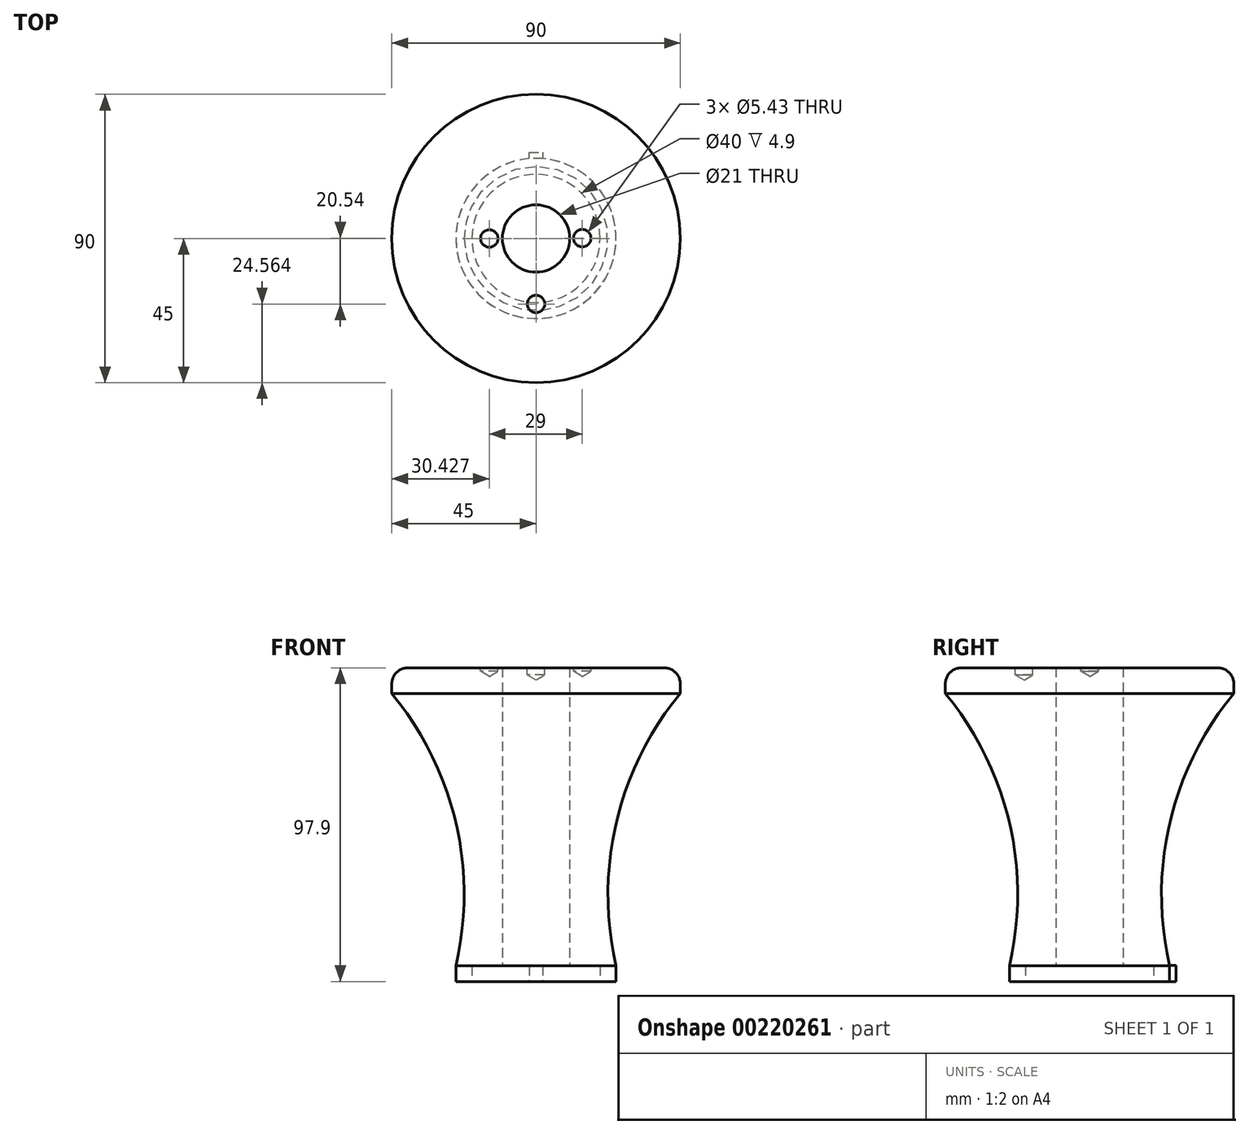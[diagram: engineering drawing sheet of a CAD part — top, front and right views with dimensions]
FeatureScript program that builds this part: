
annotation { "Feature Type Name" : "Feature", "Feature Type Description" : "" }
export const myFeature = defineFeature(function(context is Context, id is Id, definition is map)
    precondition{}
    {
        {
            var Q0;
            Q0=qCreatedBy(makeId("Front.planeOp"),FACE);
            var sketch = newSketch(context, id + "F0", { "sketchPlane" : qUnion([Q0])});
            skLineSegment(sketch, "E0", {"start": v(25, 0) * mm, "end": v(4, 0) * mm});
            skLineSegment(sketch, "E1", {"start": v(4, 0) * mm, "end": v(4, 60) * mm});
            skLineSegment(sketch, "E2", {"start": v(10, 85) * mm, "end": v(45, 85) * mm});
            skArc(sketch, "E3", {"start": v(45, 85) * mm, "mid": v(25.06, 44.84) * mm, "end": v(25, 0) * mm});
            skArc(sketch, "E4", {"start": v(10, 85) * mm, "mid": v(5.52, 72.85) * mm, "end": v(4, 60) * mm});
            skSolve(sketch);
        }
        {
            var Q0;
            Q0=qCreatedBy(makeId("Front.planeOp"),FACE);
            var sketch = newSketch(context, id + "F1", { "sketchPlane" : qUnion([Q0])});
            skLineSegment(sketch, "E5", {"start": v(0, 0) * mm, "end": v(0, 50.34) * mm});
            skSolve(sketch);
        }
        {
            var Q0;
            Q0=makeQuery(id+"F0.imprint","IMPRINT",FACE,{"disambiguationData":[TD([[makeQuery(id+"F0.imprint","IMPRINT",EDGE,{"derivedFrom":sQuery(id+"F0.wireOp",EDGE,"E0")}),-1.0]])]});
            var Q1;
            Q1=sQuery(id+"F1.wireOp",EDGE,"E5");
            revolve(context, id + "F2", {"entities" : qUnion([Q0]), "axis" : qUnion([Q1]), "revolveType" : RevolveType.FULL});
        }
        {
            var Q0;
            Q0=makeQuery(id+"F2.opRevolve","SWEPT_FACE",FACE,{"disambiguationData":[OSD([sQuery(id+"F0.wireOp",EDGE,"E0")])]});
            extrude(context, id + "F3", {"entities" : qUnion([Q0]), "operationType" : NewBodyOperationType.ADD, "depth" : 4.9 * mm});
        }
        {
            var Q0;
            Q0=makeQuery(id+"F3.opExtrude","CAP_FACE",FACE,{"disambiguationData":[OSD([sQuery(id+"F0.wireOp",EDGE,"E0")])],"isStart":false});
            var sketch = newSketch(context, id + "F4", { "sketchPlane" : qUnion([Q0])});
            skCircle(sketch, "E6", {"center": v(0, 0) * mm, "radius": 20 * mm});
            skSolve(sketch);
        }
        {
            var Q0;
            Q0=makeQuery(id+"F4.imprint","IMPRINT",FACE,{"disambiguationData":[TD([[makeQuery(id+"F4.imprint","IMPRINT",EDGE,{"derivedFrom":sQuery(id+"F4.wireOp",EDGE,"E6")}),1.0]])]});
            var Q1;
            Q1=sQuery(id+"F4.wireOp",EDGE,"E6");
            extrude(context, id + "F5", {"entities" : qUnion([Q0]), "operationType" : NewBodyOperationType.REMOVE, "surfaceEntities" : qUnion([Q1]), "oppositeDirection" : true, "depth" : 4.9 * mm});
        }
        {
            var Q0;
            Q0=makeQuery(id+"F2.opRevolve","SWEPT_FACE",FACE,{"disambiguationData":[OSD([sQuery(id+"F0.wireOp",EDGE,"E2")])]});
            extrude(context, id + "F6", {"entities" : qUnion([Q0]), "operationType" : NewBodyOperationType.ADD, "depth" : 8 * mm});
        }
        {
            var Q0;
            Q0=makeQuery(id+"F6.opExtrude","CAP_EDGE",EDGE,{"disambiguationData":[OSD([sQuery(id+"F0.wireOp",EDGE,"E2"),sQuery(id+"F0.wireOp",EDGE,"E3")])],"isStart":false});
            fillet(context, id + "F7", {"entities" : qUnion([Q0]), "radius" : 5 * mm, "tangentPropagation" : true, "allowEdgeOverflow" : false});
        }
        {
            var Q0;
            Q0=makeQuery(id+"F6.opExtrude","CAP_FACE",FACE,{"disambiguationData":[OSD([sQuery(id+"F0.wireOp",EDGE,"E2")])],"isStart":false});
            var sketch = newSketch(context, id + "F8", { "sketchPlane" : qUnion([Q0])});
            skPoint(sketch, "E7", {"position": v(0, -20.44) * mm});
            skPoint(sketch, "E8", {"position": v(-14.57, 0) * mm});
            skPoint(sketch, "E9", {"position": v(14.43, 0.1) * mm});
            skSolve(sketch);
        }
        {
            var Q0;
            Q0=sQuery(id+"F8.wireOp",VERTEX,"E9");
            var Q1;
            Q1=sQuery(id+"F8.wireOp",VERTEX,"E8");
            var Q2;
            Q2=makeQuery(id+"F2.opRevolve","SWEPT_BODY",BODY,{"disambiguationData":[OSD([sQuery(id+"F0.wireOp",EDGE,"E0"),sQuery(id+"F0.wireOp",EDGE,"E1"),sQuery(id+"F0.wireOp",EDGE,"E2"),sQuery(id+"F0.wireOp",EDGE,"E3"),sQuery(id+"F0.wireOp",EDGE,"E4")])]});
            hole(context, id + "F9", {"style" : HoleStyle.SIMPLE, "endStyle" : HoleEndStyle.BLIND, "holeDiameter" : 5.43 * mm, "holeDepth" : 1.1 * mm, "startFromSketch" : true, "locations" : qUnion([Q0, Q1]), "scope" : qUnion([Q2])});
        }
        {
            var Q0;
            Q0=sQuery(id+"F8.wireOp",VERTEX,"E7");
            var Q1;
            Q1=makeQuery(id+"F2.opRevolve","SWEPT_BODY",BODY,{"disambiguationData":[OSD([sQuery(id+"F0.wireOp",EDGE,"E0"),sQuery(id+"F0.wireOp",EDGE,"E1"),sQuery(id+"F0.wireOp",EDGE,"E2"),sQuery(id+"F0.wireOp",EDGE,"E3"),sQuery(id+"F0.wireOp",EDGE,"E4")])]});
            hole(context, id + "F10", {"style" : HoleStyle.SIMPLE, "endStyle" : HoleEndStyle.BLIND, "holeDiameter" : 5.43 * mm, "holeDepth" : 2.2 * mm, "startFromSketch" : true, "locations" : qUnion([Q0]), "scope" : qUnion([Q1])});
        }
        {
            var Q0;
            Q0=qCreatedBy(makeId("Top.planeOp"),FACE);
            var sketch = newSketch(context, id + "F11", { "sketchPlane" : qUnion([Q0])});
            skCircle(sketch, "E10", {"center": v(0, 0) * mm, "radius": 10.5 * mm});
            skSolve(sketch);
        }
        {
            var Q0;
            Q0=qSketchRegion(id+"F11",true);
            extrude(context, id + "F12", {"entities" : qUnion([Q0]), "operationType" : NewBodyOperationType.REMOVE, "depth" : 100 * mm});
        }
        {
            var Q0;
            Q0=makeQuery(id+"F4.imprint","IMPRINT",FACE,{"disambiguationData":[TD([[makeQuery(id+"F4.imprint","IMPRINT",EDGE,{"derivedFrom":sQuery(id+"F4.wireOp",EDGE,"E6")}),-1.0]])]});
            var sketch = newSketch(context, id + "F13", { "sketchPlane" : qUnion([Q0])});
            skArc(sketch, "E11", {"start": v(-2.12, -24.9) * mm, "mid": v(0, -25) * mm, "end": v(2.13, -24.9) * mm});
            skLineSegment(sketch, "E12", {"start": v(0, 0) * mm, "end": v(0, -36.79) * mm, "construction": true});
            skLineSegment(sketch, "E13", {"start": v(-2.12, -24.9) * mm, "end": v(-2.12, -26.9) * mm});
            skLineSegment(sketch, "E14", {"start": v(-2.12, -26.9) * mm, "end": v(2.13, -26.9) * mm});
            skLineSegment(sketch, "E15", {"start": v(2.13, -26.9) * mm, "end": v(2.13, -24.9) * mm});
            skSolve(sketch);
        }
        {
            var Q0;
            Q0=qSketchRegion(id+"F13",true);
            extrude(context, id + "F14", {"entities" : qUnion([Q0]), "operationType" : NewBodyOperationType.ADD, "oppositeDirection" : true, "depth" : 5 * mm});
        }
    });
